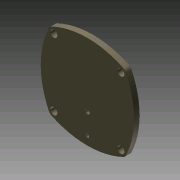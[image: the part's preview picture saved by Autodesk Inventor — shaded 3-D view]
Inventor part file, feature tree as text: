
AUTODESK INVENTOR PART (.ipt)
format: ipt  version: 2011 (Build 150239000, 239)  size: 151,040 bytes
history: native  units: in
note: dims shown in document units (in); Inventor stores cm internally (conversion verified against a paired STEP export)
features: extrude x3, sketch x2, revolve x1, reference x1
ambient origin geometry x8: Origin, YZ Plane, XZ Plane, XY Plane, X Axis, Y Axis, Z Axis, Center Point
bodies: Solid1 (feature_tree)
feature tree (7):
  extrude  "Extrusion1"  Depth=0.075in
  sketch  "Sketch2"  dims[d11=1.4in d13=0.1in d14=0.0in d15=0.1625in d16=0.1in d17=0.0in d18=0.125in d19=0.75in d21=0.675in d22=0.35in d23=90.0deg d36=0.25in d37=2.425in d38=2.425in d39=3.375in d40=0.1in d41=0.1in d42=0.1in d43=0.1in d44=2.6693in d45=2.6693in d46=0.425in d47=0.25in]
  extrude  "Extrusion2"  Depth=0.1in TaperAngle=0.0deg
  extrude  "Extrusion3"  Depth=0.1625in
  revolve  "Revolution1"  [1 undecoded]
  sketch  "Sketch1"  dims[d7=0.2in d8=0.0in d10=0.075in]
  reference  "Reference1"
note: 1 required parameter value undecoded (feature->parameter linkage not recoverable at this tier; creation-order binding heuristic only, values carry confidence <= 0.55)
